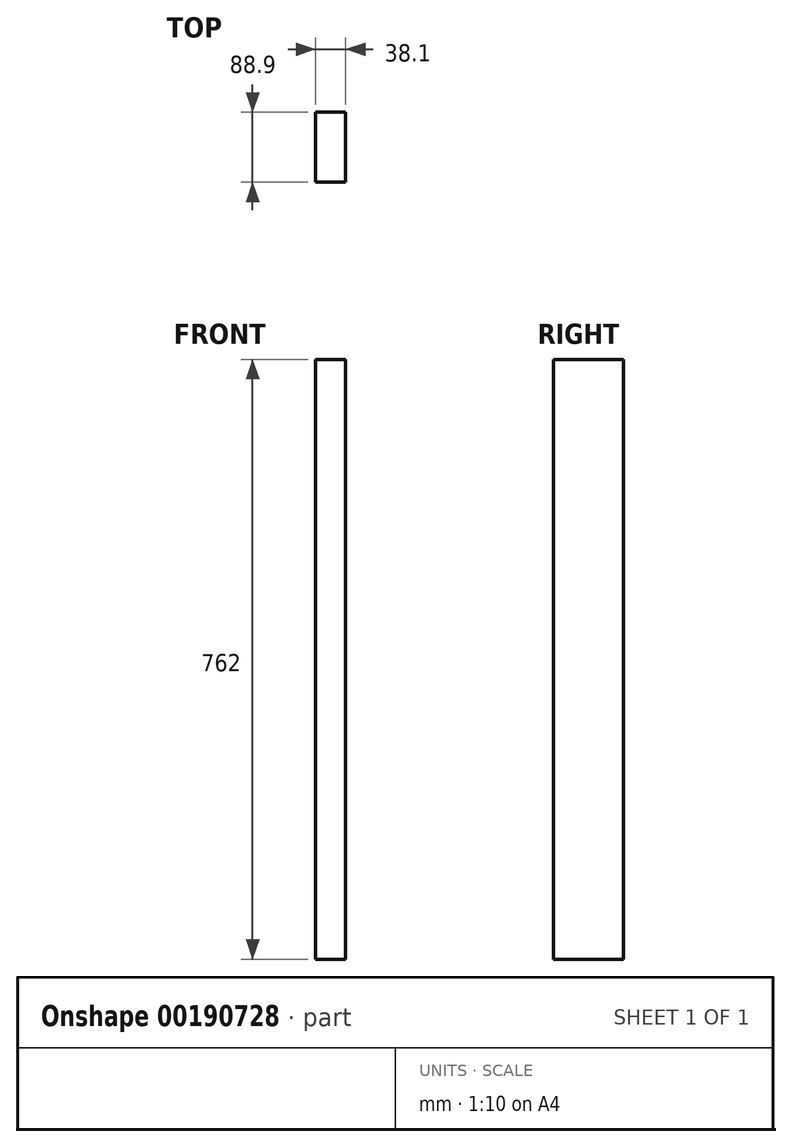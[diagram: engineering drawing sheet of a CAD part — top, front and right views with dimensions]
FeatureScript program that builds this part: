
annotation { "Feature Type Name" : "Feature", "Feature Type Description" : "" }
export const myFeature = defineFeature(function(context is Context, id is Id, definition is map)
    precondition{}
    {
        {
            var Q0;
            Q0=qCreatedBy(makeId("Top.planeOp"),FACE);
            var sketch = newSketch(context, id + "F0", { "sketchPlane" : qUnion([Q0])});
            skLineSegment(sketch, "E0.bottom", {"start": v(0, 0) * mm, "end": v(38.1, 0) * mm});
            skLineSegment(sketch, "E0.top", {"start": v(0, 88.9) * mm, "end": v(38.1, 88.9) * mm});
            skLineSegment(sketch, "E0.left", {"start": v(0, 0) * mm, "end": v(0, 88.9) * mm});
            skLineSegment(sketch, "E0.right", {"start": v(38.1, 0) * mm, "end": v(38.1, 88.9) * mm});
            skSolve(sketch);
        }
        {
            var Q0;
            Q0 = qSketchRegion(id + "F0", true);
            extrude(context, id + "F1", {"entities" : qUnion([Q0]), "depth" : 762 * mm});
        }
    });
